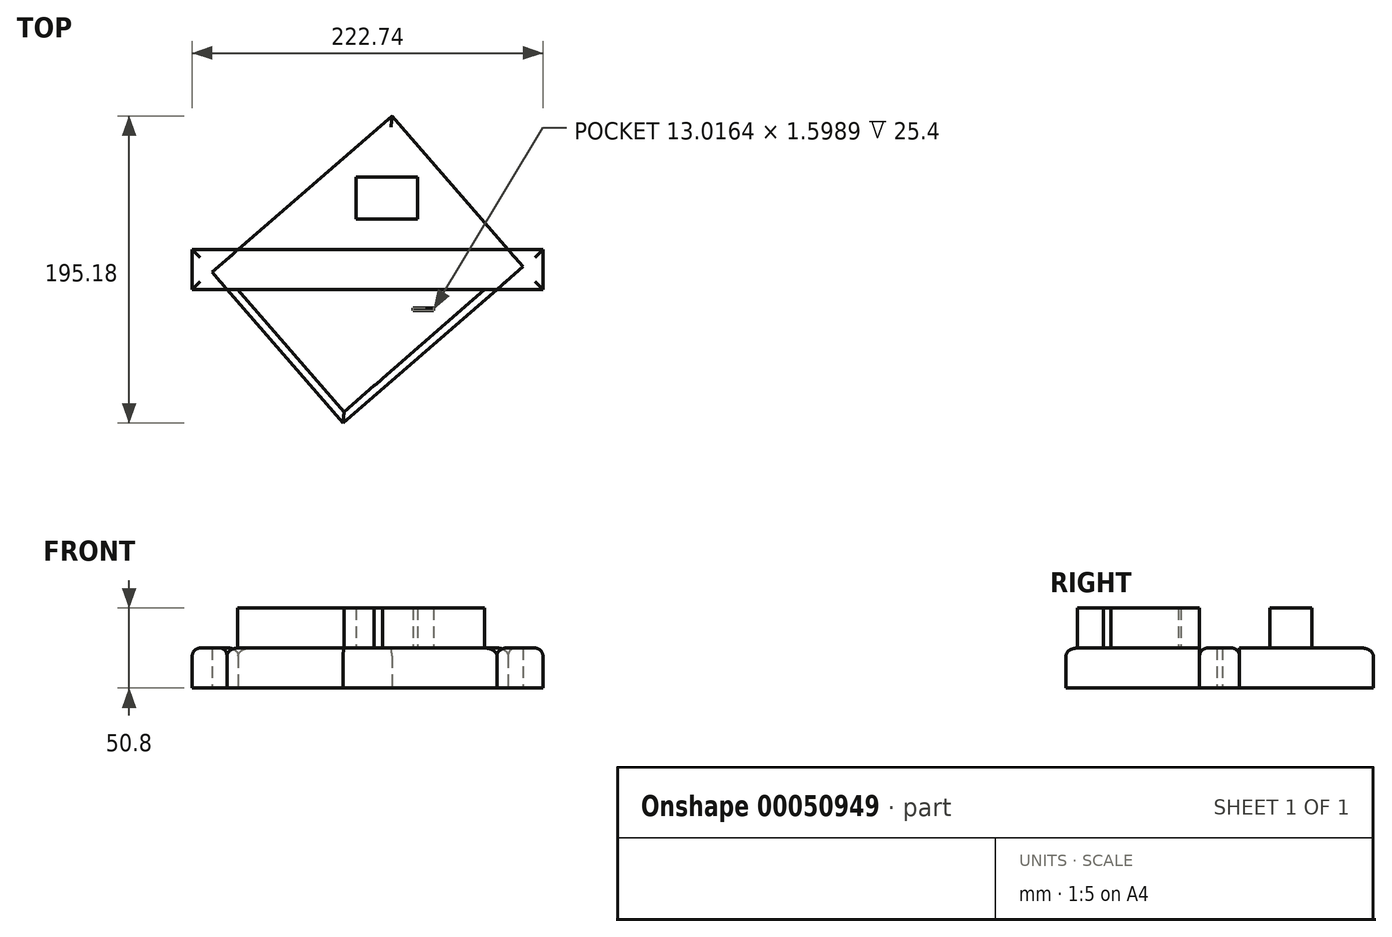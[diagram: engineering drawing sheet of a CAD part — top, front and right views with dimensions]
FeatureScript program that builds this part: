
annotation { "Feature Type Name" : "Feature", "Feature Type Description" : "" }
export const myFeature = defineFeature(function(context is Context, id is Id, definition is map)
    precondition{}
    {
        {
            var Q0;
            Q0=qCreatedBy(makeId("Top.planeOp"),FACE);
            var sketch = newSketch(context, id + "F0", { "sketchPlane" : qUnion([Q0])});
            skLineSegment(sketch, "E0.bottom", {"start": v(-111.37, -25.4) * mm, "end": v(111.37, -25.4) * mm});
            skLineSegment(sketch, "E0.top", {"start": v(-111.37, 0) * mm, "end": v(111.37, 0) * mm});
            skLineSegment(sketch, "E0.left", {"start": v(-111.37, -25.4) * mm, "end": v(-111.37, 0) * mm});
            skLineSegment(sketch, "E0.right", {"start": v(111.37, -25.4) * mm, "end": v(111.37, 0) * mm});
            skLineSegment(sketch, "E1", {"start": v(-98.79, -14.46) * mm, "end": v(-15.45, -110.29) * mm});
            skLineSegment(sketch, "E2", {"start": v(-15.45, -110.29) * mm, "end": v(98.79, -10.94) * mm});
            skLineSegment(sketch, "E3", {"start": v(98.79, -10.94) * mm, "end": v(15.45, 84.89) * mm});
            skLineSegment(sketch, "E4", {"start": v(-98.79, -14.46) * mm, "end": v(15.45, 84.89) * mm});
            skSolve(sketch);
        }
        {
            var Q0;
            {var subQ5=sQuery(id+"F0.wireOp",EDGE,"E0.left");Q0=makeQuery(id+"F0.imprint","IMPRINT",FACE,{"disambiguationData":[TD([[makeQuery(id+"F0.imprint","IMPRINT",EDGE,{"derivedFrom":subQ5}),-1.0]])]});}
            var Q1;
            {var subQ5=sQuery(id+"F0.wireOp",EDGE,"E0.right");Q1=makeQuery(id+"F0.imprint","IMPRINT",FACE,{"disambiguationData":[TD([[makeQuery(id+"F0.imprint","IMPRINT",EDGE,{"derivedFrom":subQ5}),1.0]])]});}
            var Q2;
            {var subQ0=sQuery(id+"F0.wireOp",EDGE,"E4");var subQ1=sQuery(id+"F0.wireOp",EDGE,"E0.top");var subQ2=makeQuery(id+"F0.imprint","INTERSECT",VERTEX,{"derivedFrom":[subQ1,subQ0]});Q2=makeQuery(id+"F0.imprint","IMPRINT",FACE,{"disambiguationData":[TD([[makeQuery(id+"F0.imprint","IMPRINT",EDGE,{"disambiguationData":[TD([[subQ2,-1.0]])],"derivedFrom":subQ1}),1.0]])]});}
            var Q3;
            {var subQ0=sQuery(id+"F0.wireOp",EDGE,"E1");var subQ1=sQuery(id+"F0.wireOp",EDGE,"E0.bottom");var subQ2=makeQuery(id+"F0.imprint","INTERSECT",VERTEX,{"derivedFrom":[subQ1,subQ0]});Q3=makeQuery(id+"F0.imprint","IMPRINT",FACE,{"disambiguationData":[TD([[makeQuery(id+"F0.imprint","IMPRINT",EDGE,{"disambiguationData":[TD([[subQ2,-1.0]])],"derivedFrom":subQ1}),-1.0]])]});}
            extrude(context, id + "F1", {"entities" : qUnion([Q0, Q1, Q2, Q3]), "depth" : 25.4 * mm});
        }
        {
            var Q0;
            {var subQ0=sQuery(id+"F0.wireOp",EDGE,"E1");Q0=makeQuery(id+"F1.opExtrude","CAP_EDGE",EDGE,{"disambiguationData":[OSD([subQ0]),TDD([makeQuery(id+"F0.imprint","IMPRINT",EDGE,{"disambiguationData":[TD([[makeQuery(id+"F0.imprint","INTERSECT",VERTEX,{"derivedFrom":[subQ0,sQuery(id+"F0.wireOp",EDGE,"E2")]}),1.0]])],"derivedFrom":subQ0})])],"isStart":false});}
            var Q1;
            {var subQ0=sQuery(id+"F0.wireOp",EDGE,"E2");Q1=makeQuery(id+"F1.opExtrude","CAP_EDGE",EDGE,{"disambiguationData":[OSD([subQ0]),TDD([makeQuery(id+"F0.imprint","IMPRINT",EDGE,{"disambiguationData":[TD([[makeQuery(id+"F0.imprint","INTERSECT",VERTEX,{"derivedFrom":[sQuery(id+"F0.wireOp",EDGE,"E1"),subQ0]}),-1.0]])],"derivedFrom":subQ0})])],"isStart":false});}
            var Q2;
            {var subQ0=sQuery(id+"F0.wireOp",EDGE,"E0.bottom");Q2=makeQuery(id+"F1.opExtrude","CAP_EDGE",EDGE,{"disambiguationData":[OSD([subQ0]),TDD([makeQuery(id+"F0.imprint","IMPRINT",EDGE,{"disambiguationData":[TD([[makeQuery(id+"F0.imprint","INTERSECT",VERTEX,{"derivedFrom":[subQ0,sQuery(id+"F0.wireOp",EDGE,"E0.right")]}),1.0]])],"derivedFrom":subQ0})])],"isStart":false});}
            var Q3;
            Q3=makeQuery(id+"F1.opExtrude","CAP_EDGE",EDGE,{"disambiguationData":[OSD([sQuery(id+"F0.wireOp",EDGE,"E0.right")])],"isStart":false});
            var Q4;
            {var subQ0=sQuery(id+"F0.wireOp",EDGE,"E3");Q4=makeQuery(id+"F1.opExtrude","CAP_EDGE",EDGE,{"disambiguationData":[OSD([subQ0]),TDD([makeQuery(id+"F0.imprint","IMPRINT",EDGE,{"disambiguationData":[TD([[makeQuery(id+"F0.imprint","INTERSECT",VERTEX,{"derivedFrom":[subQ0,sQuery(id+"F0.wireOp",EDGE,"E4")]}),1.0]])],"derivedFrom":subQ0})])],"isStart":false});}
            var Q5;
            {var subQ0=sQuery(id+"F0.wireOp",EDGE,"E0.top");Q5=makeQuery(id+"F1.opExtrude","CAP_EDGE",EDGE,{"disambiguationData":[OSD([subQ0]),TDD([makeQuery(id+"F0.imprint","IMPRINT",EDGE,{"disambiguationData":[TD([[makeQuery(id+"F0.imprint","INTERSECT",VERTEX,{"derivedFrom":[subQ0,sQuery(id+"F0.wireOp",EDGE,"E0.right")]}),1.0]])],"derivedFrom":subQ0})])],"isStart":false});}
            var Q6;
            {var subQ0=sQuery(id+"F0.wireOp",EDGE,"E4");Q6=makeQuery(id+"F1.opExtrude","CAP_EDGE",EDGE,{"disambiguationData":[OSD([subQ0]),TDD([makeQuery(id+"F0.imprint","IMPRINT",EDGE,{"disambiguationData":[TD([[makeQuery(id+"F0.imprint","INTERSECT",VERTEX,{"derivedFrom":[sQuery(id+"F0.wireOp",EDGE,"E3"),subQ0]}),1.0]])],"derivedFrom":subQ0})])],"isStart":false});}
            var Q7;
            {var subQ0=sQuery(id+"F0.wireOp",EDGE,"E0.top");Q7=makeQuery(id+"F1.opExtrude","CAP_EDGE",EDGE,{"disambiguationData":[OSD([subQ0]),TDD([makeQuery(id+"F0.imprint","IMPRINT",EDGE,{"disambiguationData":[TD([[makeQuery(id+"F0.imprint","INTERSECT",VERTEX,{"derivedFrom":[subQ0,sQuery(id+"F0.wireOp",EDGE,"E0.left")]}),-1.0]])],"derivedFrom":subQ0})])],"isStart":false});}
            var Q8;
            Q8=makeQuery(id+"F1.opExtrude","CAP_EDGE",EDGE,{"disambiguationData":[OSD([sQuery(id+"F0.wireOp",EDGE,"E0.left")])],"isStart":false});
            var Q9;
            {var subQ0=sQuery(id+"F0.wireOp",EDGE,"E0.bottom");Q9=makeQuery(id+"F1.opExtrude","CAP_EDGE",EDGE,{"disambiguationData":[OSD([subQ0]),TDD([makeQuery(id+"F0.imprint","IMPRINT",EDGE,{"disambiguationData":[TD([[makeQuery(id+"F0.imprint","INTERSECT",VERTEX,{"derivedFrom":[subQ0,sQuery(id+"F0.wireOp",EDGE,"E0.left")]}),-1.0]])],"derivedFrom":subQ0})])],"isStart":false});}
            fillet(context, id + "F2", {"entities" : qUnion([Q0, Q1, Q2, Q3, Q4, Q5, Q6, Q7, Q8, Q9]), "radius" : 5.08 * mm, "tangentPropagation" : true, "allowEdgeOverflow" : false});
        }
        {
            var Q0;
            Q0=makeQuery(id+"F1.opExtrude","CAP_FACE",FACE,{"disambiguationData":[OSD([sQuery(id+"F0.wireOp",EDGE,"E0.top"),sQuery(id+"F0.wireOp",EDGE,"E3"),sQuery(id+"F0.wireOp",EDGE,"E4")])],"isStart":false});
            var sketch = newSketch(context, id + "F3", { "sketchPlane" : qUnion([Q0])});
            skCircle(sketch, "E5", {"center": v(-9.63, -65.15) * mm, "radius": 25.4 * mm});
            skSolve(sketch);
        }
        {
            var Q0;
            Q0=makeQuery(id+"F3.imprint","IMPRINT",FACE,{"disambiguationData":[TD([[makeQuery(id+"F3.imprint","IMPRINT",EDGE,{"derivedFrom":sQuery(id+"F3.wireOp",EDGE,"E5")}),1.0]])]});
            extrude(context, id + "F4", {"entities" : qUnion([Q0]), "operationType" : NewBodyOperationType.ADD, "depth" : 25.4 * mm});
        }
        {
            var Q0;
            Q0=makeQuery(id+"F1.opExtrude","CAP_FACE",FACE,{"disambiguationData":[OSD([sQuery(id+"F0.wireOp",EDGE,"E0.top"),sQuery(id+"F0.wireOp",EDGE,"E3"),sQuery(id+"F0.wireOp",EDGE,"E4")])],"isStart":false});
            var sketch = newSketch(context, id + "F5", { "sketchPlane" : qUnion([Q0])});
            skLineSegment(sketch, "E6.bottom", {"start": v(-7.36, 19.32) * mm, "end": v(31.62, 19.32) * mm});
            skLineSegment(sketch, "E6.top", {"start": v(-7.36, 45.95) * mm, "end": v(31.62, 45.95) * mm});
            skLineSegment(sketch, "E6.left", {"start": v(-7.36, 19.32) * mm, "end": v(-7.36, 45.95) * mm});
            skLineSegment(sketch, "E6.right", {"start": v(31.62, 19.32) * mm, "end": v(31.62, 45.95) * mm});
            skSolve(sketch);
        }
        {
            var Q0;
            Q0=makeQuery(id+"F5.imprint","IMPRINT",FACE,{"disambiguationData":[TD([[makeQuery(id+"F5.imprint","IMPRINT",EDGE,{"derivedFrom":sQuery(id+"F5.wireOp",EDGE,"E6.bottom")}),1.0]])]});
            extrude(context, id + "F6", {"entities" : qUnion([Q0]), "operationType" : NewBodyOperationType.ADD, "depth" : 25.4 * mm});
        }
        {
            var Q0;
            Q0=makeQuery(id+"F1.opExtrude","CAP_FACE",FACE,{"disambiguationData":[OSD([sQuery(id+"F0.wireOp",EDGE,"E0.bottom"),sQuery(id+"F0.wireOp",EDGE,"E1"),sQuery(id+"F0.wireOp",EDGE,"E2")])],"isStart":false});
            var sketch = newSketch(context, id + "F7", { "sketchPlane" : qUnion([Q0])});
            skPoint(sketch, "E7.oppositeSnap0", {"position": v(41.95, -53.64) * mm});
            skLineSegment(sketch, "E7.bottom", {"start": v(28.94, -38.88) * mm, "end": v(41.95, -38.88) * mm});
            skLineSegment(sketch, "E7.top", {"start": v(28.94, -37.28) * mm, "end": v(41.95, -37.28) * mm});
            skLineSegment(sketch, "E7.left", {"start": v(28.94, -38.88) * mm, "end": v(28.94, -37.28) * mm});
            skLineSegment(sketch, "E7.right", {"start": v(41.95, -38.88) * mm, "end": v(41.95, -37.28) * mm});
            skSolve(sketch);
        }
        {
            var Q0;
            Q0=makeQuery(id+"F7.imprint","IMPRINT",FACE,{"disambiguationData":[TD([[makeQuery(id+"F7.imprint","IMPRINT",EDGE,{"derivedFrom":sQuery(id+"F7.wireOp",EDGE,"E7.bottom")}),-1.0]])]});
            extrude(context, id + "F8", {"entities" : qUnion([Q0]), "operationType" : NewBodyOperationType.ADD, "depth" : 25.4 * mm, "offsetDistance" : 25.4 * mm});
        }
    });
